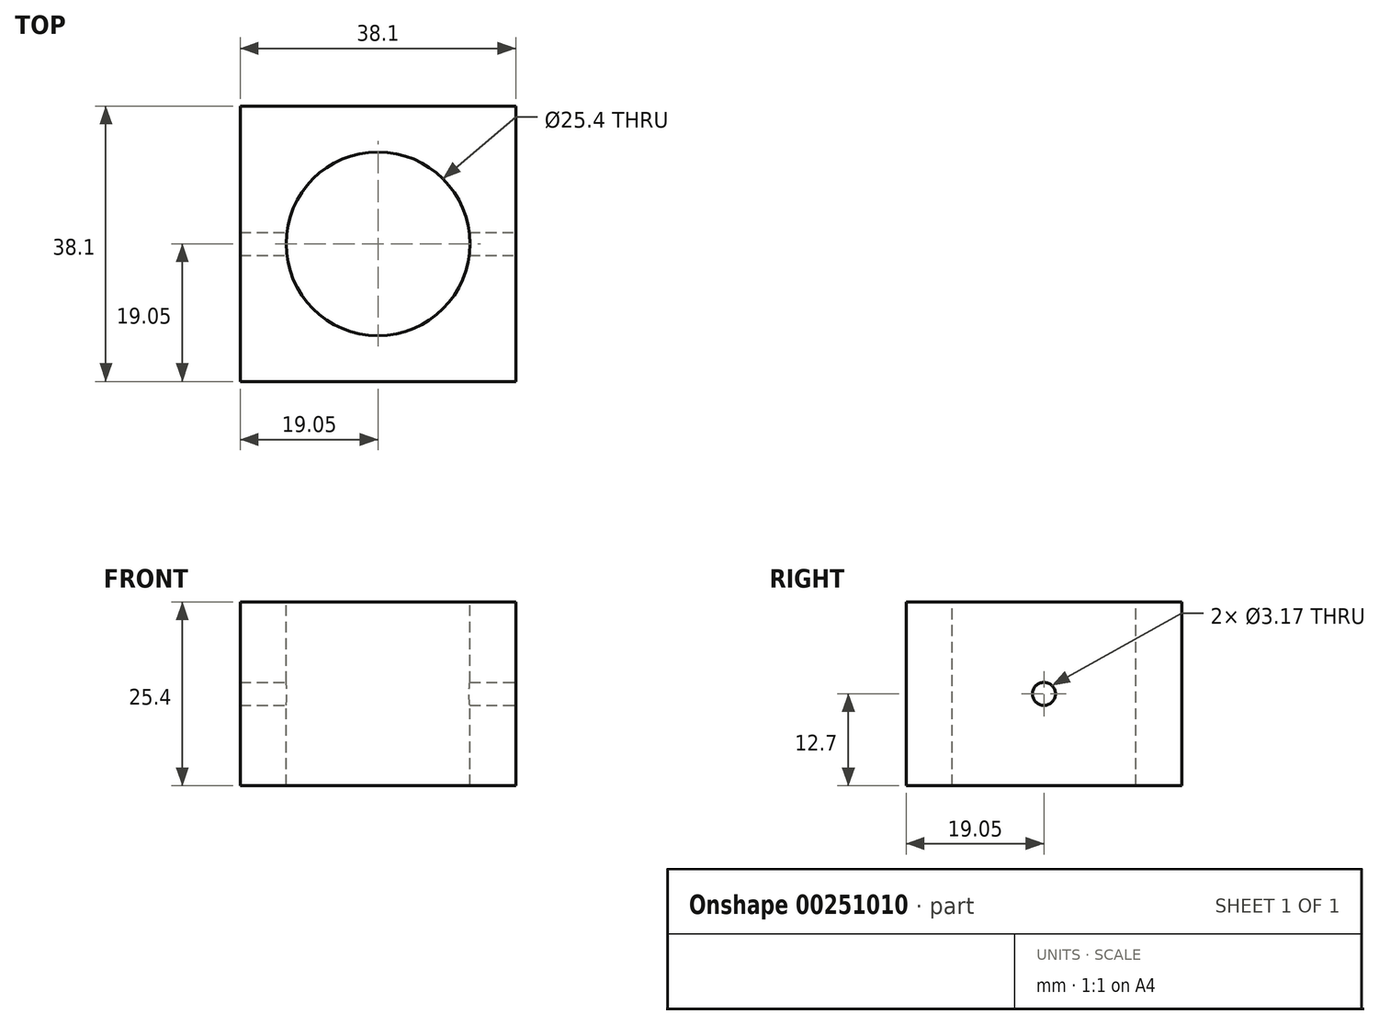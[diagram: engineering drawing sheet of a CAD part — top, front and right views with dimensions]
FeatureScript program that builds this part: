
annotation { "Feature Type Name" : "Feature", "Feature Type Description" : "" }
export const myFeature = defineFeature(function(context is Context, id is Id, definition is map)
    precondition{}
    {
        {
            var Q0;
            Q0=qCreatedBy(makeId("Top.planeOp"),FACE);
            var sketch = newSketch(context, id + "F0", { "sketchPlane" : qUnion([Q0])});
            skLineSegment(sketch, "E0.bottom", {"start": v(0, 0) * mm, "end": v(38.1, 0) * mm});
            skLineSegment(sketch, "E0.top", {"start": v(0, 38.1) * mm, "end": v(38.1, 38.1) * mm});
            skLineSegment(sketch, "E0.left", {"start": v(0, 0) * mm, "end": v(0, 38.1) * mm});
            skLineSegment(sketch, "E0.right", {"start": v(38.1, 0) * mm, "end": v(38.1, 38.1) * mm});
            skSolve(sketch);
        }
        {
            var Q0;
            Q0=makeQuery(id+"F0.imprint","IMPRINT",FACE,{"disambiguationData":[TD([[makeQuery(id+"F0.imprint","IMPRINT",EDGE,{"derivedFrom":sQuery(id+"F0.wireOp",EDGE,"E0.bottom")}),1.0]])]});
            extrude(context, id + "F1", {"entities" : qUnion([Q0]), "depth" : 25.4 * mm});
        }
        {
            var Q0;
            Q0=makeQuery(id+"F1.opExtrude","SWEPT_FACE",FACE,{"disambiguationData":[OSD([sQuery(id+"F0.wireOp",EDGE,"E0.right")])]});
            var sketch = newSketch(context, id + "F2", { "sketchPlane" : qUnion([Q0])});
            skCircle(sketch, "E1", {"center": v(19.05, 12.7) * mm, "radius": 1.59 * mm});
            skSolve(sketch);
        }
        {
            var Q0;
            Q0=makeQuery(id+"F2.imprint","IMPRINT",FACE,{"disambiguationData":[TD([[makeQuery(id+"F2.imprint","IMPRINT",EDGE,{"derivedFrom":sQuery(id+"F2.wireOp",EDGE,"E1")}),1.0]])]});
            extrude(context, id + "F3", {"entities" : qUnion([Q0]), "operationType" : NewBodyOperationType.REMOVE, "oppositeDirection" : true, "depth" : 38.1 * mm});
        }
        {
            var Q0;
            Q0=makeQuery(id+"F1.opExtrude","CAP_FACE",FACE,{"disambiguationData":[OSD([sQuery(id+"F0.wireOp",EDGE,"E0.bottom"),sQuery(id+"F0.wireOp",EDGE,"E0.top"),sQuery(id+"F0.wireOp",EDGE,"E0.left"),sQuery(id+"F0.wireOp",EDGE,"E0.right")])],"isStart":false});
            var sketch = newSketch(context, id + "F4", { "sketchPlane" : qUnion([Q0])});
            skCircle(sketch, "E2", {"center": v(19.05, 19.05) * mm, "radius": 12.7 * mm});
            skSolve(sketch);
        }
        {
            var Q0;
            Q0=makeQuery(id+"F4.imprint","IMPRINT",FACE,{"disambiguationData":[TD([[makeQuery(id+"F4.imprint","IMPRINT",EDGE,{"derivedFrom":sQuery(id+"F4.wireOp",EDGE,"E2")}),1.0]])]});
            extrude(context, id + "F5", {"entities" : qUnion([Q0]), "operationType" : NewBodyOperationType.REMOVE, "oppositeDirection" : true, "depth" : 25.4 * mm});
        }
    });
